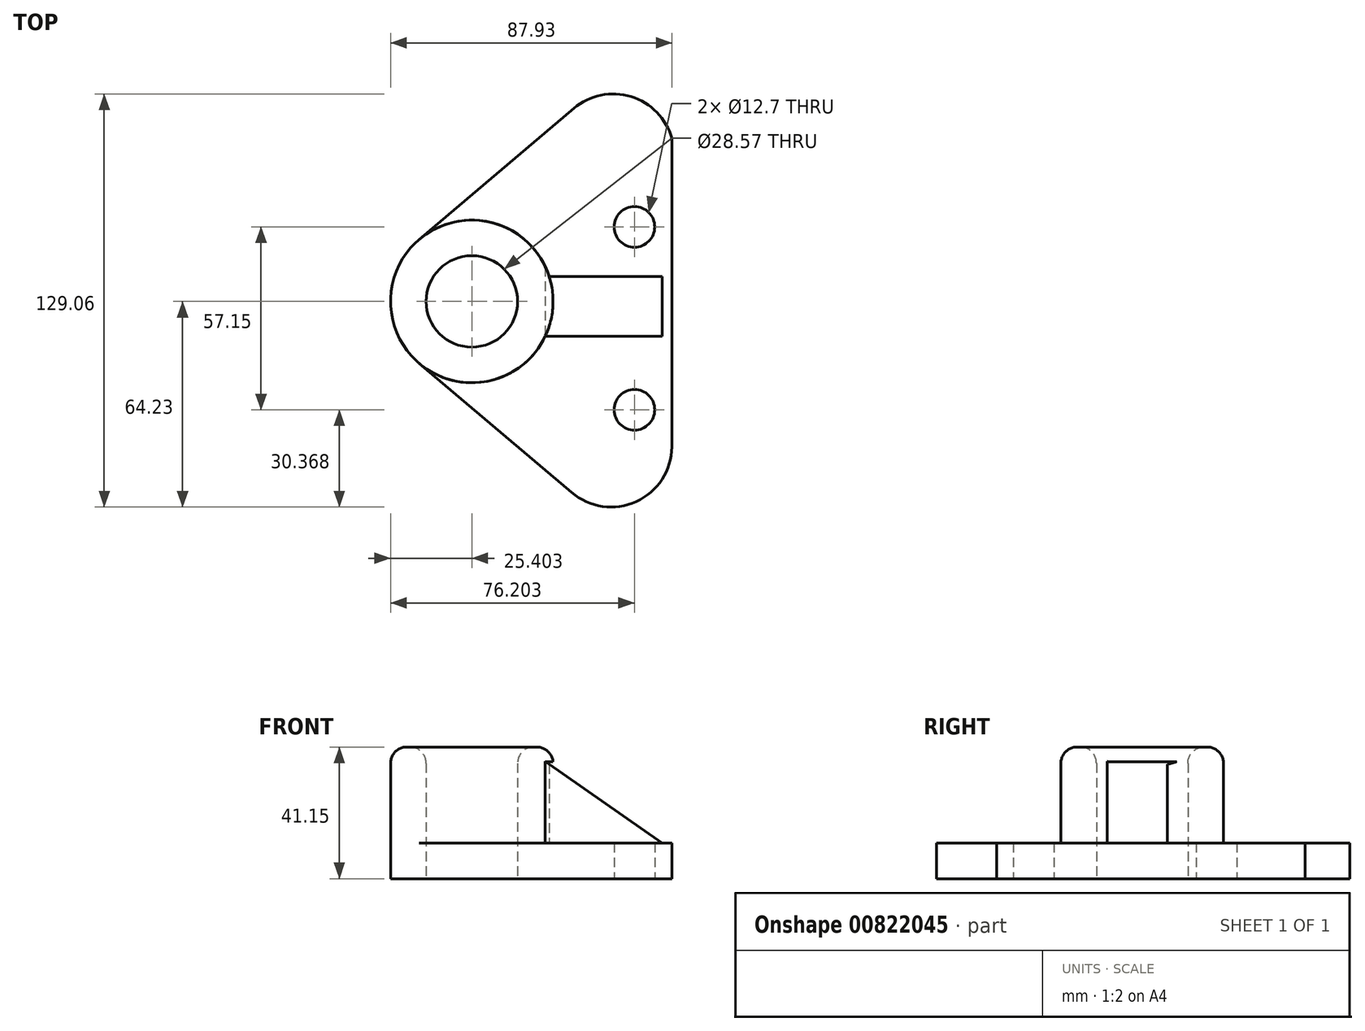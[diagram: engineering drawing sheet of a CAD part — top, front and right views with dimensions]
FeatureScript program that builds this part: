
annotation { "Feature Type Name" : "Feature", "Feature Type Description" : "" }
export const myFeature = defineFeature(function(context is Context, id is Id, definition is map)
    precondition{}
    {
        {
            var Q0;
            Q0=qCreatedBy(makeId("Top.planeOp"),FACE);
            var sketch = newSketch(context, id + "F0", { "sketchPlane" : qUnion([Q0])});
            skCircle(sketch, "E0", {"center": v(-46.4, 0) * mm, "radius": 25.4 * mm});
            skCircle(sketch, "E1", {"center": v(-46.4, 0) * mm, "radius": 14.29 * mm});
            skCircle(sketch, "E2", {"center": v(4.4, -33.86) * mm, "radius": 6.35 * mm});
            skCircle(sketch, "E3", {"center": v(4.4, 23.29) * mm, "radius": 6.35 * mm});
            skLineSegment(sketch, "E4", {"start": v(-62.83, -19.38) * mm, "end": v(-15.25, -59.71) * mm});
            skArc(sketch, "E5", {"start": v(-15.25, -59.71) * mm, "mid": v(4.96, -62.53) * mm, "end": v(16.12, -45.46) * mm});
            skPoint(sketch, "E6.orphan", {"position": v(4.4, 53.16) * mm});
            skLineSegment(sketch, "E7", {"start": v(-62.83, 19.38) * mm, "end": v(-14.54, 60.31) * mm});
            skArc(sketch, "E8", {"start": v(16.12, 50.93) * mm, "mid": v(3.35, 64) * mm, "end": v(-14.54, 60.31) * mm});
            skLineSegment(sketch, "E9", {"start": v(16.12, 50.93) * mm, "end": v(16.12, -45.46) * mm});
            skSolve(sketch);
        }
        {
            var Q0;
            Q0=makeQuery(id+"F0.imprint","IMPRINT",FACE,{"disambiguationData":[TD([[makeQuery(id+"F0.imprint","IMPRINT",EDGE,{"derivedFrom":sQuery(id+"F0.wireOp",EDGE,"E1")}),-1.0]])]});
            extrude(context, id + "F1", {"entities" : qUnion([Q0]), "depth" : 41.15 * mm, "offsetDistance" : 25.4 * mm});
        }
        {
            var Q0;
            Q0=makeQuery(id+"F0.imprint","IMPRINT",FACE,{"disambiguationData":[TD([[makeQuery(id+"F0.imprint","IMPRINT",EDGE,{"derivedFrom":sQuery(id+"F0.wireOp",EDGE,"E2")}),-1.0]])]});
            extrude(context, id + "F2", {"entities" : qUnion([Q0]), "operationType" : NewBodyOperationType.ADD, "depth" : 11.18 * mm, "offsetDistance" : 25.4 * mm});
        }
        {
            var Q0;
            Q0=makeQuery(id+"F2.opExtrude","CAP_FACE",FACE,{"disambiguationData":[OSD([sQuery(id+"F0.wireOp",EDGE,"E0"),sQuery(id+"F0.wireOp",EDGE,"E2"),sQuery(id+"F0.wireOp",EDGE,"E3"),sQuery(id+"F0.wireOp",EDGE,"E4"),sQuery(id+"F0.wireOp",EDGE,"E5"),sQuery(id+"F0.wireOp",EDGE,"E7"),sQuery(id+"F0.wireOp",EDGE,"E8"),sQuery(id+"F0.wireOp",EDGE,"E9")])],"isStart":false});
            var sketch = newSketch(context, id + "F3", { "sketchPlane" : qUnion([Q0])});
            skLineSegment(sketch, "E10.bottom", {"start": v(-23.45, -10.88) * mm, "end": v(13.03, -10.88) * mm});
            skLineSegment(sketch, "E10.top", {"start": v(-23.45, 7.84) * mm, "end": v(13.03, 7.84) * mm});
            skLineSegment(sketch, "E10.right", {"start": v(13.03, -10.88) * mm, "end": v(13.03, 7.84) * mm});
            skSolve(sketch);
        }
        {
            var Q0;
            {var subQ0=sQuery(id+"F3.wireOp",EDGE,"E10.bottom");Q0=makeQuery(id+"F3.imprint","IMPRINT",FACE,{"disambiguationData":[TD([[makeQuery(id+"F3.imprint","IMPRINT",EDGE,{"derivedFrom":subQ0}),1.0]])]});}
            extrude(context, id + "F4", {"entities" : qUnion([Q0]), "operationType" : NewBodyOperationType.ADD, "depth" : 25.4 * mm, "offsetDistance" : 25.4 * mm});
        }
        {
            var Q0;
            Q0=makeQuery(id+"F4.opExtrude","SWEPT_FACE",FACE,{"disambiguationData":[OSD([sQuery(id+"F3.wireOp",EDGE,"E10.bottom")])]});
            var sketch = newSketch(context, id + "F5", { "sketchPlane" : qUnion([Q0])});
            skLineSegment(sketch, "E11", {"start": v(-23.45, 36.58) * mm, "end": v(13.03, 11.18) * mm});
            skSolve(sketch);
        }
        {
            var Q0;
            Q0=makeQuery(id+"F5.imprint","IMPRINT",FACE,{"disambiguationData":[TD([[makeQuery(id+"F5.imprint","IMPRINT",EDGE,{"derivedFrom":sQuery(id+"F5.wireOp",EDGE,"E11")}),1.0]])]});
            extrude(context, id + "F6", {"entities" : qUnion([Q0]), "operationType" : NewBodyOperationType.REMOVE, "oppositeDirection" : true, "depth" : 51.05 * mm, "offsetDistance" : 25.4 * mm});
        }
        {
            var Q0;
            Q0=makeQuery(id+"F1.opExtrude","CAP_EDGE",EDGE,{"disambiguationData":[OSD([sQuery(id+"F0.wireOp",EDGE,"E0")])],"isStart":false});
            var Q1;
            Q1=makeQuery(id+"F4.opExtrude","CAP_EDGE",EDGE,{"disambiguationData":[OSD([sQuery(id+"F3.wireOp",EDGE,"E10.bottom")])],"isStart":true});
            var Q2;
            Q2=makeQuery(id+"F4.opExtrude","CAP_EDGE",EDGE,{"disambiguationData":[OSD([sQuery(id+"F3.wireOp",EDGE,"E10.top")])],"isStart":true});
            var Q3;
            Q3=makeQuery(id+"F1.opExtrude","CAP_EDGE",EDGE,{"disambiguationData":[OSD([sQuery(id+"F0.wireOp",EDGE,"E1")])],"isStart":false});
            fillet(context, id + "F7", {"entities" : qUnion([Q0, Q1, Q2, Q3]), "radius" : 5.08 * mm, "tangentPropagation" : true, "allowEdgeOverflow" : false});
        }
    });
